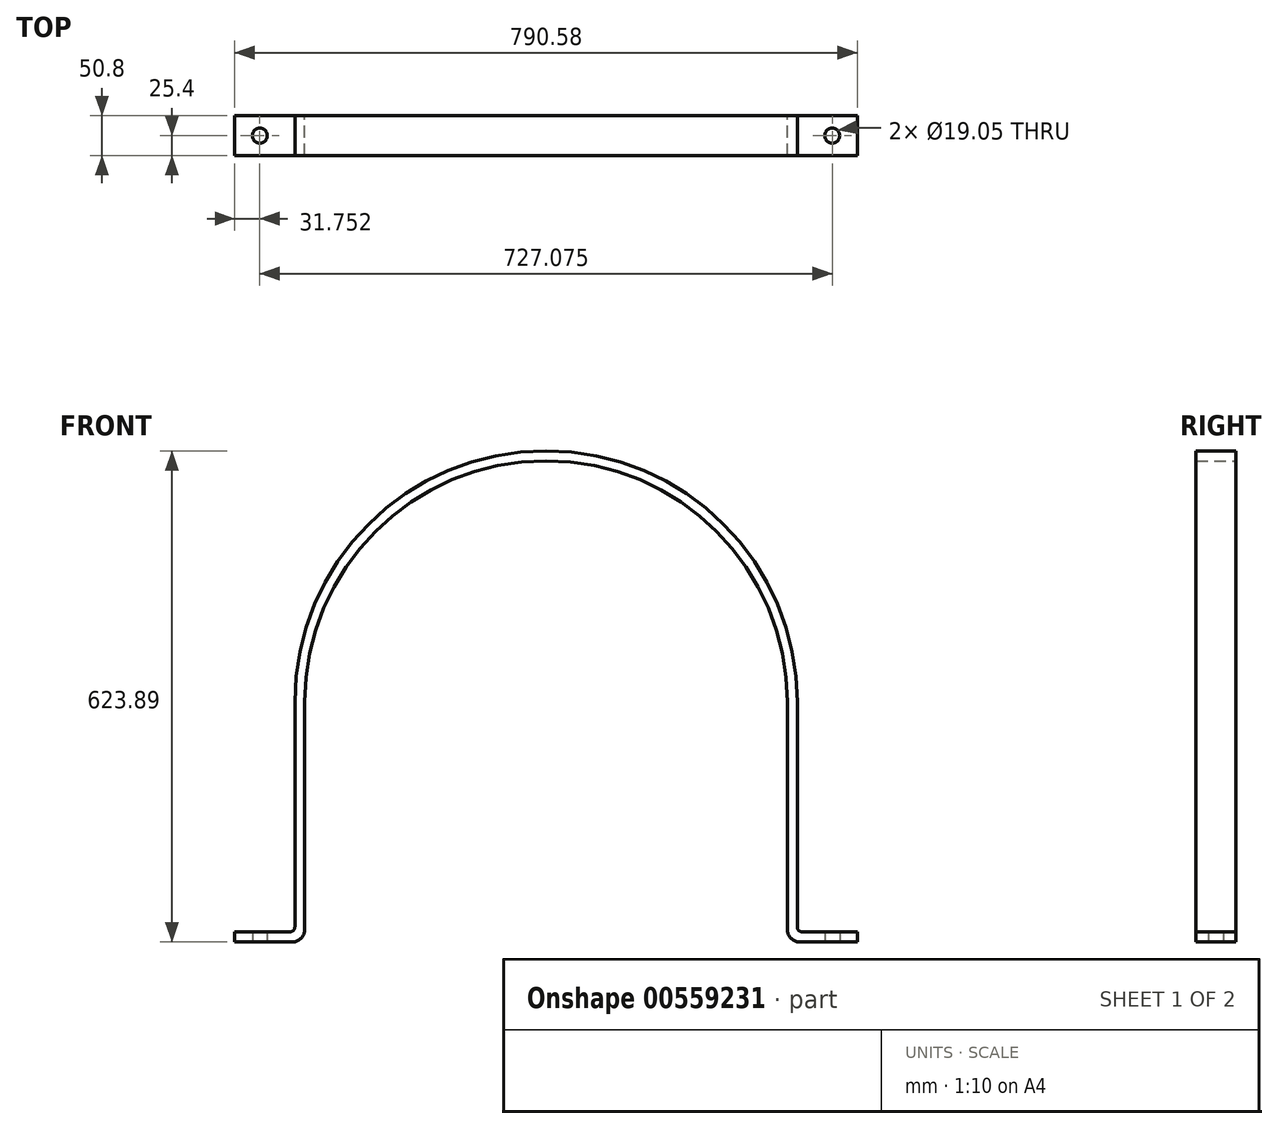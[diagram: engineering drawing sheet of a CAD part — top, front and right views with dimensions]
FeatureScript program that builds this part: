
annotation { "Feature Type Name" : "Feature", "Feature Type Description" : "" }
export const myFeature = defineFeature(function(context is Context, id is Id, definition is map)
    precondition{}
    {
        {
            var Q0;
            Q0=qCreatedBy(makeId("Front.planeOp"),FACE);
            var sketch = newSketch(context, id + "F0", { "sketchPlane" : qUnion([Q0])});
            skLineSegment(sketch, "E0.bottom", {"start": v(395.29, -304.8) * mm, "end": v(306.39, -304.8) * mm});
            skLineSegment(sketch, "E0.top", {"start": v(395.29, -292.1) * mm, "end": v(319.09, -292.1) * mm});
            skLineSegment(sketch, "E0.left", {"start": v(395.29, -304.8) * mm, "end": v(395.29, -292.1) * mm});
            skLineSegment(sketch, "E0.right", {"start": v(-395.29, -304.8) * mm, "end": v(-395.29, -292.1) * mm});
            skLineSegment(sketch, "E1", {"start": v(-306.39, 0) * mm, "end": v(-306.39, -304.8) * mm});
            skLineSegment(sketch, "E2", {"start": v(-319.09, 0) * mm, "end": v(-319.09, -292.1) * mm});
            skLineSegment(sketch, "E3", {"start": v(306.39, 0) * mm, "end": v(306.39, -304.8) * mm});
            skLineSegment(sketch, "E4", {"start": v(319.09, 0) * mm, "end": v(319.09, -292.1) * mm});
            skLineSegment(sketch, "E5", {"start": v(319.09, -292.1) * mm, "end": v(324.17, -286.68) * mm});
            skArc(sketch, "E6.trimOffspring", {"start": v(319.09, 0) * mm, "mid": v(0, 319.09) * mm, "end": v(-319.09, 0) * mm});
            skArc(sketch, "E7.trimOffspring", {"start": v(306.39, 0) * mm, "mid": v(0, 306.39) * mm, "end": v(-306.39, 0) * mm});
            skLineSegment(sketch, "E8.trimOffspring", {"start": v(-319.09, -292.1) * mm, "end": v(-395.29, -292.1) * mm});
            skLineSegment(sketch, "E9.trimOffspring", {"start": v(-306.39, -304.8) * mm, "end": v(-395.29, -304.8) * mm});
            skSolve(sketch);
        }
        {
            var Q0;
            Q0 = qSketchRegion(id + "F0", true);
            extrude(context, id + "F1", {"entities" : qUnion([Q0]), "endBound" : BoundingType.SYMMETRIC, "depth" : 50.8 * mm, "offsetDistance" : 25.4 * mm});
        }
        {
            var Q0;
            Q0=makeQuery(id+"F1.opExtrude","SWEPT_EDGE",EDGE,{"disambiguationData":[OSD([sQuery(id+"F0.wireOp",EDGE,"E2"),sQuery(id+"F0.wireOp",EDGE,"E8.trimOffspring")])]});
            var Q1;
            Q1=makeQuery(id+"F1.opExtrude","SWEPT_EDGE",EDGE,{"disambiguationData":[OSD([sQuery(id+"F0.wireOp",EDGE,"E0.top"),sQuery(id+"F0.wireOp",EDGE,"E4")])]});
            fillet(context, id + "F2", {"entities" : qUnion([Q0, Q1]), "radius" : 6.35 * mm, "tangentPropagation" : true, "allowEdgeOverflow" : false});
        }
        {
            var Q0;
            Q0=makeQuery(id+"F1.opExtrude","SWEPT_EDGE",EDGE,{"disambiguationData":[OSD([sQuery(id+"F0.wireOp",EDGE,"E0.bottom"),sQuery(id+"F0.wireOp",EDGE,"E3")])]});
            var Q1;
            Q1=makeQuery(id+"F1.opExtrude","SWEPT_EDGE",EDGE,{"disambiguationData":[OSD([sQuery(id+"F0.wireOp",EDGE,"E1"),sQuery(id+"F0.wireOp",EDGE,"E9.trimOffspring")])]});
            fillet(context, id + "F3", {"entities" : qUnion([Q0, Q1]), "radius" : 15.88 * mm, "tangentPropagation" : true, "allowEdgeOverflow" : false});
        }
        {
            var Q0;
            Q0=makeQuery(id+"F1.opExtrude","SWEPT_FACE",FACE,{"disambiguationData":[OSD([sQuery(id+"F0.wireOp",EDGE,"E0.bottom")])]});
            var sketch = newSketch(context, id + "F4", { "sketchPlane" : qUnion([Q0])});
            skCircle(sketch, "E10", {"center": v(-363.54, 0) * mm, "radius": 9.53 * mm});
            skCircle(sketch, "E11.MirrorC", {"center": v(363.54, 0) * mm, "radius": 9.53 * mm});
            skSolve(sketch);
        }
        {
            var Q0;
            Q0 = qSketchRegion(id + "F4", true);
            extrude(context, id + "F5", {"entities" : qUnion([Q0]), "operationType" : NewBodyOperationType.REMOVE, "oppositeDirection" : true, "depth" : 25.4 * mm, "offsetDistance" : 25.4 * mm});
        }
    });
